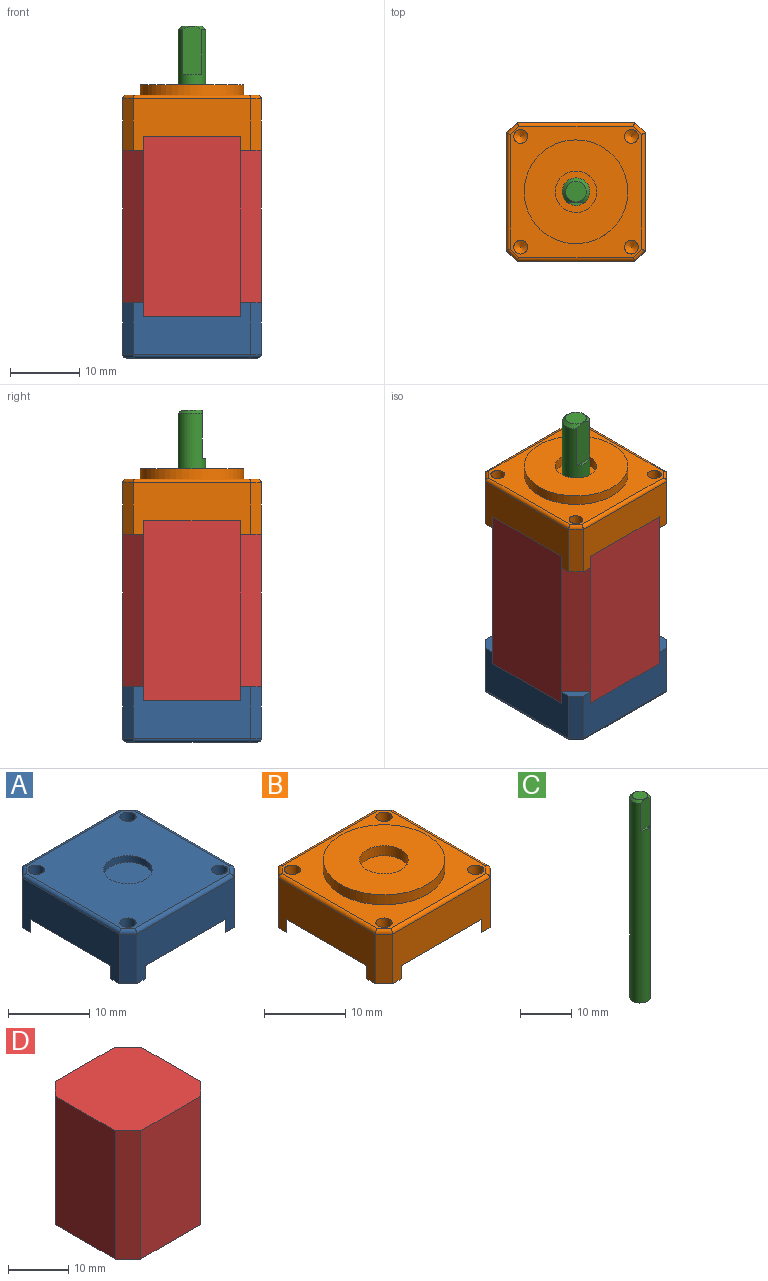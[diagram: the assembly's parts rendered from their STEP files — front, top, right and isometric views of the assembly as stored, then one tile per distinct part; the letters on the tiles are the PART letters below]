
ASSEMBLY  parts=4 mates=3
PART A: 36 faces, bbox 20x20x8 mm
  f0: plane 20x20mm, normal (0,0,-1), area 382mm2, adj f1,f3,f5,f7,f12,f14,f16,f18
  f1: plane 17x7.5mm, normal (0,1,0), area 99.5mm2, adj f0,f2,f8,f14,f15,f18,f19,f30
  f2: plane 7.5x1.5mm, normal (-0.71,0.71,0), area 15.9mm2, adj f1,f3,f19,f32
  f3: plane 17x7.5mm, normal (-1,0,0), area 99.5mm2, adj f0,f2,f4,f16,f17,f18,f19,f34
  f4: plane 7.5x1.5mm, normal (-0.71,-0.71,0), area 15.9mm2, adj f3,f5,f17,f35
  f5: plane 17x7.5mm, normal (0,-1,0), area 99.5mm2, adj f0,f4,f6,f12,f13,f16,f17,f33
  f6: plane 7.5x1.5mm, normal (0.71,-0.71,0), area 15.9mm2, adj f5,f7,f13,f31
  f7: plane 17x7.5mm, normal (1,0,0), area 99.5mm2, adj f0,f6,f8,f12,f13,f14,f15,f29
  f8: plane 7.5x1.5mm, normal (0.71,0.71,0), area 15.9mm2, adj f1,f7,f15,f28
  f9: plane 19x19mm, normal (0,0,1), area 317.2mm2, adj f10,f21,f23,f25,f27,f28,f29,f30
  f10: cylinder r=3mm len=6mm, axis (0,0,1), area 18.8mm2, adj f9,f11
  f11: plane 6x6mm, normal (0,0,1), area 28.3mm2, adj f10
  f12: plane 3x3mm, normal (-0.71,0.71,0), area 8.5mm2, adj f0,f5,f7,f13
  f13: plane 3x3mm, normal (0,0,-1), area 3.4mm2, adj f5,f6,f7,f12
  f14: plane 3x3mm, normal (-0.71,-0.71,0), area 8.5mm2, adj f0,f1,f7,f15
  f15: plane 3x3mm, normal (0,0,-1), area 3.4mm2, adj f1,f7,f8,f14
  f16: plane 3x3mm, normal (0.71,0.71,0), area 8.5mm2, adj f0,f3,f5,f17
  f17: plane 3x3mm, normal (0,0,-1), area 3.4mm2, adj f3,f4,f5,f16
  f18: plane 3x3mm, normal (0.71,-0.71,0), area 8.5mm2, adj f0,f1,f3,f19
  f19: plane 3x3mm, normal (0,0,-1), area 3.4mm2, adj f1,f2,f3,f18
  f20: cone r=0mm half-angle=59deg, axis (0,0,1), area 3.7mm2, adj f21
  f21: cylinder r=1mm len=3mm, axis (0,0,1), area 18.8mm2, adj f9,f20
  f22: cone r=0mm half-angle=59deg, axis (0,0,1), area 3.7mm2, adj f23
  f23: cylinder r=1mm len=3mm, axis (0,0,1), area 18.8mm2, adj f9,f22
  f24: cone r=0mm half-angle=59deg, axis (0,0,1), area 3.7mm2, adj f25
  f25: cylinder r=1mm len=3mm, axis (0,0,1), area 18.8mm2, adj f9,f24
  f26: cone r=0mm half-angle=59deg, axis (0,0,1), area 3.7mm2, adj f27
  f27: cylinder r=1mm len=3mm, axis (0,0,1), area 18.8mm2, adj f9,f26
  f28: cylinder r=0.5mm len=1.85mm, axis (-0.71,0.71,0), area 1.5mm2, adj f8,f9,f29,f30
  f29: cylinder r=0.5mm len=17mm, axis (0,1,0), area 13.2mm2, adj f7,f9,f28,f31
  f30: cylinder r=0.5mm len=17mm, axis (-1,0,0), area 13.2mm2, adj f1,f9,f28,f32
  f31: cylinder r=0.5mm len=1.85mm, axis (0.71,0.71,0), area 1.5mm2, adj f6,f9,f29,f33
  f32: cylinder r=0.5mm len=1.85mm, axis (-0.71,-0.71,0), area 1.5mm2, adj f2,f9,f30,f34
  f33: cylinder r=0.5mm len=17mm, axis (1,0,0), area 13.2mm2, adj f5,f9,f31,f35
  f34: cylinder r=0.5mm len=17mm, axis (0,-1,0), area 13.2mm2, adj f3,f9,f32,f35
  f35: cylinder r=0.5mm len=1.85mm, axis (0.71,-0.71,0), area 1.5mm2, adj f4,f9,f33,f34
PART B: 38 faces, bbox 20x20x9.5 mm
  f0: plane 20x20mm, normal (0,0,-1), area 382mm2, adj f1,f3,f5,f7,f14,f16,f18,f20
  f1: plane 17x7.5mm, normal (0,-1,0), area 99.5mm2, adj f0,f2,f8,f16,f17,f20,f21,f37
  f2: plane 7.5x1.5mm, normal (0.71,-0.71,0), area 15.9mm2, adj f1,f3,f17,f35
  f3: plane 17x7.5mm, normal (1,0,0), area 99.5mm2, adj f0,f2,f4,f14,f15,f16,f17,f33
  f4: plane 7.5x1.5mm, normal (0.71,0.71,0), area 15.9mm2, adj f3,f5,f15,f31
  f5: plane 17x7.5mm, normal (0,1,0), area 99.5mm2, adj f0,f4,f6,f14,f15,f18,f19,f30
  f6: plane 7.5x1.5mm, normal (-0.71,0.71,0), area 15.9mm2, adj f5,f7,f19,f32
  f7: plane 17x7.5mm, normal (-1,0,0), area 99.5mm2, adj f0,f6,f8,f18,f19,f20,f21,f34
  f8: plane 7.5x1.5mm, normal (-0.71,-0.71,0), area 15.9mm2, adj f1,f7,f21,f36
  f9: plane 19x19mm, normal (0,0,1), area 168.8mm2, adj f11,f23,f25,f27,f29,f30,f31,f32
  f10: cylinder r=3mm len=6mm, axis (0,0,-1), area 28.3mm2, adj f12,f13
  f11: cylinder r=7.5mm len=15mm, axis (0,0,-1), area 70.7mm2, adj f9,f12
  f12: plane 15x15mm, normal (0,0,1), area 148.4mm2, adj f10,f11
  f13: plane 6x6mm, normal (0,0,1), area 28.3mm2, adj f10
  f14: plane 3x3mm, normal (-0.71,-0.71,0), area 8.5mm2, adj f0,f3,f5,f15
  f15: plane 3x3mm, normal (0,0,-1), area 3.4mm2, adj f3,f4,f5,f14
  f16: plane 3x3mm, normal (-0.71,0.71,0), area 8.5mm2, adj f0,f1,f3,f17
  f17: plane 3x3mm, normal (0,0,-1), area 3.4mm2, adj f1,f2,f3,f16
  f18: plane 3x3mm, normal (0.71,-0.71,0), area 8.5mm2, adj f0,f5,f7,f19
  f19: plane 3x3mm, normal (0,0,-1), area 3.4mm2, adj f5,f6,f7,f18
  f20: plane 3x3mm, normal (0.71,0.71,0), area 8.5mm2, adj f0,f1,f7,f21
  f21: plane 3x3mm, normal (0,0,-1), area 3.4mm2, adj f1,f7,f8,f20
  f22: cone r=0mm half-angle=59deg, axis (0,0,1), area 3.7mm2, adj f23
  f23: cylinder r=1mm len=3mm, axis (0,0,1), area 18.8mm2, adj f9,f22
  f24: cone r=0mm half-angle=59deg, axis (0,0,1), area 3.7mm2, adj f25
  f25: cylinder r=1mm len=3mm, axis (0,0,1), area 18.8mm2, adj f9,f24
  f26: cone r=0mm half-angle=59deg, axis (0,0,1), area 3.7mm2, adj f27
  f27: cylinder r=1mm len=3mm, axis (0,0,1), area 18.8mm2, adj f9,f26
  f28: cone r=0mm half-angle=59deg, axis (0,0,1), area 3.7mm2, adj f29
  f29: cylinder r=1mm len=3mm, axis (0,0,1), area 18.8mm2, adj f9,f28
  f30: cylinder r=0.5mm len=17mm, axis (-1,0,0), area 13.2mm2, adj f5,f9,f31,f32
  f31: cylinder r=0.5mm len=1.85mm, axis (-0.71,0.71,0), area 1.5mm2, adj f4,f9,f30,f33
  f32: cylinder r=0.5mm len=1.85mm, axis (-0.71,-0.71,0), area 1.5mm2, adj f6,f9,f30,f34
  f33: cylinder r=0.5mm len=17mm, axis (0,1,0), area 13.2mm2, adj f3,f9,f31,f35
  f34: cylinder r=0.5mm len=17mm, axis (0,-1,0), area 13.2mm2, adj f7,f9,f32,f36
  f35: cylinder r=0.5mm len=1.85mm, axis (0.71,0.71,0), area 1.5mm2, adj f2,f9,f33,f37
  f36: cylinder r=0.5mm len=1.85mm, axis (0.71,-0.71,0), area 1.5mm2, adj f8,f9,f34,f37
  f37: cylinder r=0.5mm len=17mm, axis (1,0,0), area 13.2mm2, adj f1,f9,f35,f36
PART C: 6 faces, bbox 4x4x48 mm
  f0: plane 3x3mm, normal (0,0,1), area 7.1mm2, adj f4
  f1: cylinder r=2mm len=47.5mm, axis (0,0,-1), area 578.1mm2, adj f2,f3,f4,f5
  f2: plane 7x2.65mm, normal (0,-1,0), area 18.1mm2, adj f1,f3,f4
  f3: plane 2.65x0.5mm, normal (0,0,1), area 0.9mm2, adj f1,f2
  f4: cone r=1.5mm half-angle=45deg, axis (0,0,-1), area 6.5mm2, adj f0,f1,f2
  f5: plane 4x4mm, normal (0,0,-1), area 12.6mm2, adj f1
PART D: 10 faces, bbox 20x20x26 mm
  f0: plane 26x14mm, normal (0,1,0), area 364mm2, adj f1,f7,f8,f9
  f1: plane 26x3mm, normal (-0.71,0.71,0), area 110.3mm2, adj f0,f2,f8,f9
  f2: plane 26x14mm, normal (-1,0,0), area 364mm2, adj f1,f3,f8,f9
  f3: plane 26x3mm, normal (-0.71,-0.71,0), area 110.3mm2, adj f2,f4,f8,f9
  f4: plane 26x14mm, normal (0,-1,0), area 364mm2, adj f3,f5,f8,f9
  f5: plane 26x3mm, normal (0.71,-0.71,0), area 110.3mm2, adj f4,f6,f8,f9
  f6: plane 26x14mm, normal (1,0,0), area 364mm2, adj f5,f7,f8,f9
  f7: plane 26x3mm, normal (0.71,0.71,0), area 110.3mm2, adj f0,f6,f8,f9
  f8: plane 20x20mm, normal (0,0,1), area 382mm2, adj f0,f1,f2,f3,f4,f5,f6,f7
  f9: plane 20x20mm, normal (0,0,-1), area 382mm2, adj f0,f1,f2,f3,f4,f5,f6,f7
PLACE A rot(axis=(1,0,0),180deg) t=(130,0,-6)mm
PLACE B t=(80,0,32)mm
PLACE C t=(55,30,32)mm
PLACE D at identity
MATE fastened A.f10 <-> D.f9  axis (0,0,1) through (80,0,0)mm
MATE revolute C.f1 <-> B.f10  axis (0,0,1) through (80,0,32)mm
MATE fastened B.f10 <-> D.f8  axis (0,0,-1) through (80,0,26)mm
